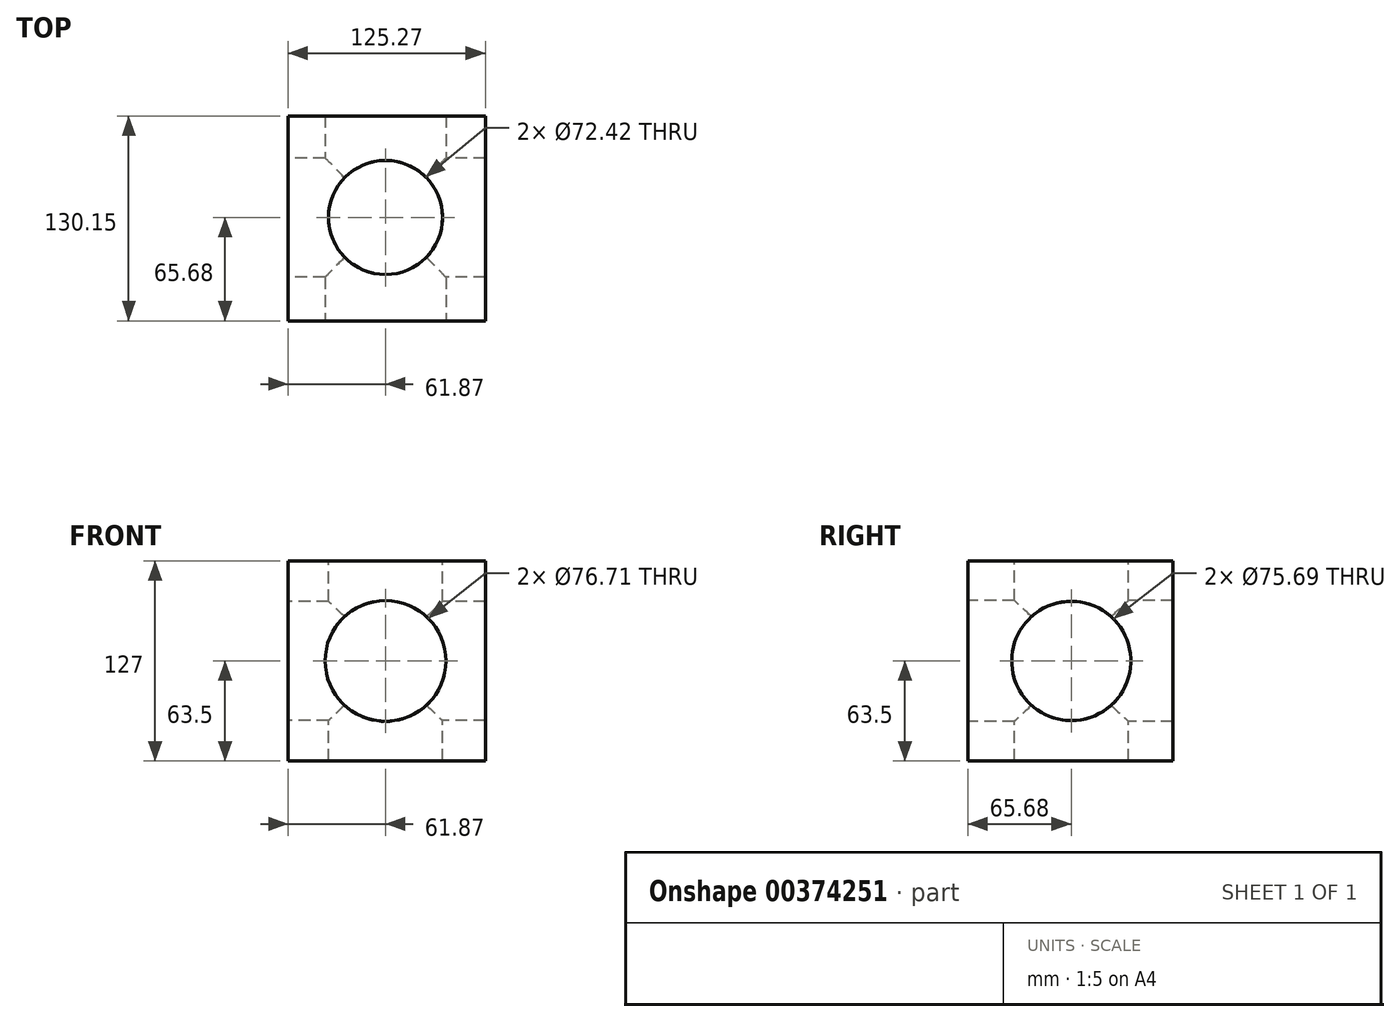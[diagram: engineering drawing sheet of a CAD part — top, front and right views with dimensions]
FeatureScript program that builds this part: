
annotation { "Feature Type Name" : "Feature", "Feature Type Description" : "" }
export const myFeature = defineFeature(function(context is Context, id is Id, definition is map)
    precondition{}
    {
        {
            var Q0;
            Q0=qCreatedBy(makeId("Top.planeOp"),FACE);
            var sketch = newSketch(context, id + "F0", { "sketchPlane" : qUnion([Q0])});
            skLineSegment(sketch, "E0.bottom", {"start": v(-61.87, 64.47) * mm, "end": v(63.4, 64.47) * mm});
            skLineSegment(sketch, "E0.top", {"start": v(-61.87, -65.68) * mm, "end": v(63.4, -65.68) * mm});
            skLineSegment(sketch, "E0.left", {"start": v(-61.87, 64.47) * mm, "end": v(-61.87, -65.68) * mm});
            skLineSegment(sketch, "E0.right", {"start": v(63.4, 64.47) * mm, "end": v(63.4, -65.68) * mm});
            skSolve(sketch);
        }
        {
            var Q0;
            Q0=makeQuery(id+"F0.imprint","IMPRINT",FACE,{"disambiguationData":[TD([[makeQuery(id+"F0.imprint","IMPRINT",EDGE,{"derivedFrom":sQuery(id+"F0.wireOp",EDGE,"E0.bottom")}),-1.0]])]});
            extrude(context, id + "F1", {"entities" : qUnion([Q0]), "endBound" : BoundingType.SYMMETRIC, "depth" : 127 * mm});
        }
        {
            var Q0;
            Q0=makeQuery(id+"F1.opExtrude","CAP_FACE",FACE,{"disambiguationData":[OSD([sQuery(id+"F0.wireOp",EDGE,"E0.bottom"),sQuery(id+"F0.wireOp",EDGE,"E0.top"),sQuery(id+"F0.wireOp",EDGE,"E0.left"),sQuery(id+"F0.wireOp",EDGE,"E0.right")])],"isStart":false});
            var sketch = newSketch(context, id + "F2", { "sketchPlane" : qUnion([Q0])});
            skCircle(sketch, "E1", {"center": v(0, 0) * mm, "radius": 36.21 * mm});
            skSolve(sketch);
        }
        {
            var Q0;
            Q0=makeQuery(id+"F2.imprint","IMPRINT",FACE,{"disambiguationData":[TD([[makeQuery(id+"F2.imprint","IMPRINT",EDGE,{"derivedFrom":sQuery(id+"F2.wireOp",EDGE,"E1")}),1.0]])]});
            extrude(context, id + "F3", {"entities" : qUnion([Q0]), "operationType" : NewBodyOperationType.REMOVE, "endBound" : BoundingType.THROUGH_ALL, "oppositeDirection" : true, "depth" : 25.4 * mm});
        }
        {
            var Q0;
            Q0=makeQuery(id+"F1.opExtrude","SWEPT_FACE",FACE,{"disambiguationData":[OSD([sQuery(id+"F0.wireOp",EDGE,"E0.left")])]});
            var sketch = newSketch(context, id + "F4", { "sketchPlane" : qUnion([Q0])});
            skCircle(sketch, "E2", {"center": v(0, 0) * mm, "radius": 37.84 * mm});
            skSolve(sketch);
        }
        {
            var Q0;
            Q0=makeQuery(id+"F4.imprint","IMPRINT",FACE,{"disambiguationData":[TD([[makeQuery(id+"F4.imprint","IMPRINT",EDGE,{"derivedFrom":sQuery(id+"F4.wireOp",EDGE,"E2")}),1.0]])]});
            extrude(context, id + "F5", {"entities" : qUnion([Q0]), "operationType" : NewBodyOperationType.REMOVE, "endBound" : BoundingType.THROUGH_ALL, "oppositeDirection" : true, "depth" : 25.4 * mm});
        }
        {
            var Q0;
            Q0=makeQuery(id+"F1.opExtrude","SWEPT_FACE",FACE,{"disambiguationData":[OSD([sQuery(id+"F0.wireOp",EDGE,"E0.top")])]});
            var sketch = newSketch(context, id + "F6", { "sketchPlane" : qUnion([Q0])});
            skCircle(sketch, "E3", {"center": v(0, 0) * mm, "radius": 38.36 * mm});
            skSolve(sketch);
        }
        {
            var Q0;
            Q0=makeQuery(id+"F6.imprint","IMPRINT",FACE,{"disambiguationData":[TD([[makeQuery(id+"F6.imprint","IMPRINT",EDGE,{"derivedFrom":sQuery(id+"F6.wireOp",EDGE,"E3")}),1.0]])]});
            extrude(context, id + "F7", {"entities" : qUnion([Q0]), "operationType" : NewBodyOperationType.REMOVE, "endBound" : BoundingType.THROUGH_ALL, "oppositeDirection" : true, "depth" : 25.4 * mm});
        }
    });
